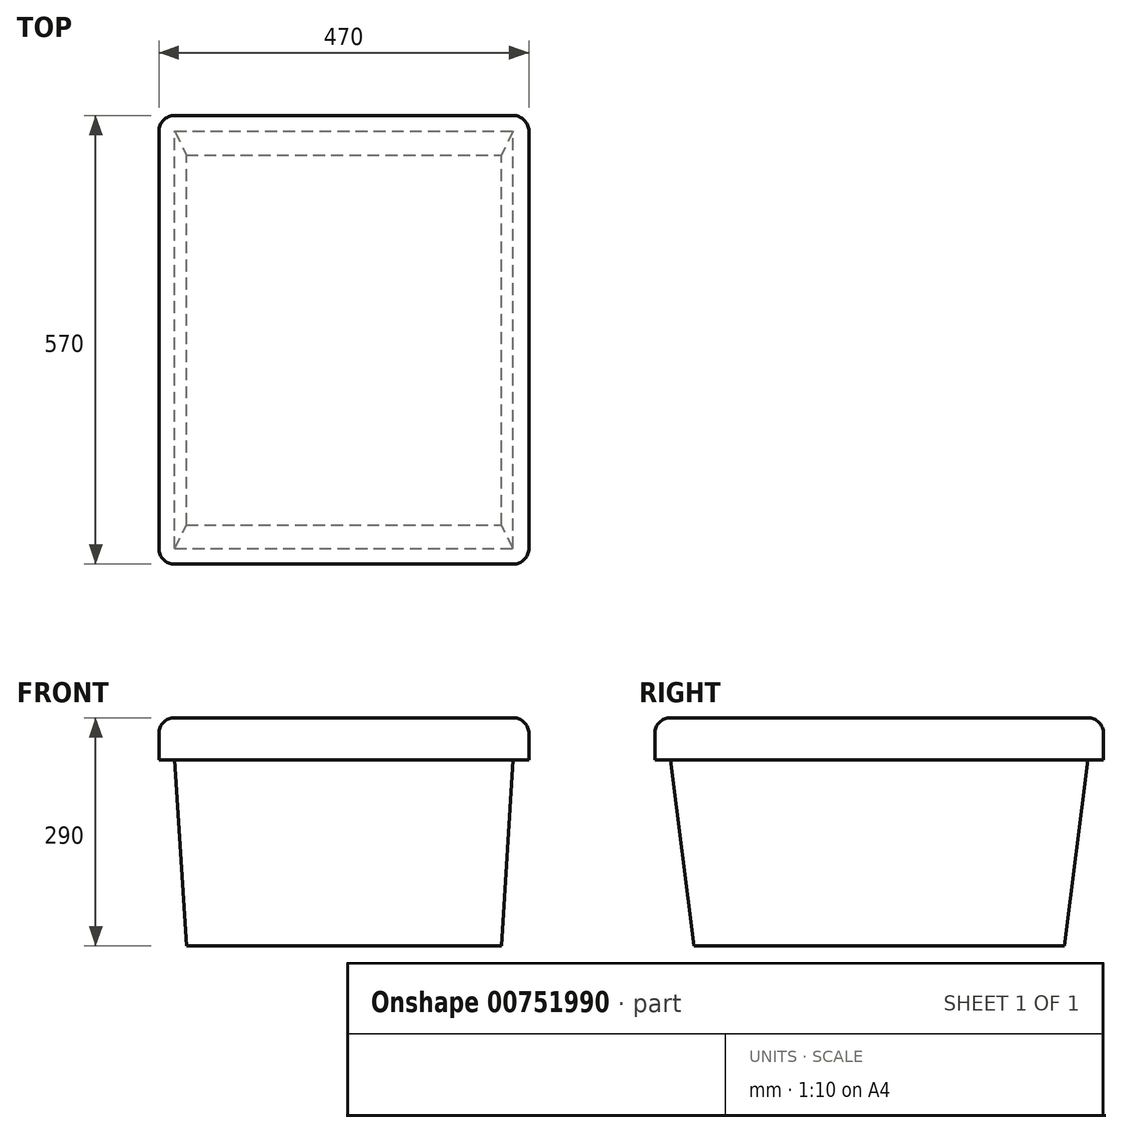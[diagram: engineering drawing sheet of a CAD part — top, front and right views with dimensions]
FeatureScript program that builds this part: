
annotation { "Feature Type Name" : "Feature", "Feature Type Description" : "" }
export const myFeature = defineFeature(function(context is Context, id is Id, definition is map)
    precondition{}
    {
        {
            var Q0;
            Q0=qCreatedBy(makeId("Front.planeOp"),FACE);
            var sketch = newSketch(context, id + "F0", { "sketchPlane" : qUnion([Q0])});
            skLineSegment(sketch, "E0.bottom", {"start": v(-35, 0) * mm, "end": v(-435, 0) * mm});
            skLineSegment(sketch, "E0.top", {"start": v(-20, 290) * mm, "end": v(-450, 290) * mm});
            skLineSegment(sketch, "E0.left", {"start": v(0, 236.3) * mm, "end": v(0, 270) * mm});
            skLineSegment(sketch, "E0.right", {"start": v(-470, 236.3) * mm, "end": v(-470, 270) * mm});
            skLineSegment(sketch, "E1", {"start": v(-470, 236.3) * mm, "end": v(-450, 236.3) * mm});
            skLineSegment(sketch, "E2", {"start": v(-450, 236.3) * mm, "end": v(-435, 0) * mm});
            skLineSegment(sketch, "E3", {"start": v(-235, 290) * mm, "end": v(-235, 0) * mm});
            skLineSegment(sketch, "E4.MirrorCS", {"start": v(-20, 236.3) * mm, "end": v(-35, 0) * mm});
            skLineSegment(sketch, "E5.MirrorCS", {"start": v(0, 236.3) * mm, "end": v(-20, 236.3) * mm});
            skPoint(sketch, "E6.orphan", {"position": v(-470, 0) * mm});
            skPoint(sketch, "E7.orphan", {"position": v(0, 0) * mm});
            skPoint(sketch, "E8.visualSharp", {"position": v(-470, 290) * mm});
            skArc(sketch, "E8.filletArc", {"start": v(-450, 290) * mm, "mid": v(-464.14, 284.14) * mm, "end": v(-470, 270) * mm});
            skPoint(sketch, "E9.visualSharp", {"position": v(0, 290) * mm});
            skArc(sketch, "E9.filletArc", {"start": v(0, 270) * mm, "mid": v(-5.86, 284.14) * mm, "end": v(-20, 290) * mm});
            skSolve(sketch);
        }
        {
            var Q0;
            Q0 = qSketchRegion(id + "F0", true);
            extrude(context, id + "F1", {"entities" : qUnion([Q0]), "depth" : 570 * mm, "offsetDistance" : 25 * mm});
        }
        {
            var Q0;
            Q0=qCreatedBy(makeId("Right.planeOp"),FACE);
            var sketch = newSketch(context, id + "F2", { "sketchPlane" : qUnion([Q0])});
            skLineSegment(sketch, "E10.0.0", {"start": v(0, 0) * mm, "end": v(0, 236.3) * mm});
            skLineSegment(sketch, "E10.0.1", {"start": v(0, 236.3) * mm, "end": v(-570, 236.3) * mm});
            skLineSegment(sketch, "E10.0.2", {"start": v(-570, 236.3) * mm, "end": v(-570, 0) * mm});
            skLineSegment(sketch, "E10.0.3", {"start": v(-570, 0) * mm, "end": v(0, 0) * mm});
            skLineSegment(sketch, "E11", {"start": v(0, 236.3) * mm, "end": v(-20, 236.3) * mm});
            skLineSegment(sketch, "E12", {"start": v(-20, 236.3) * mm, "end": v(-50, 0) * mm});
            skLineSegment(sketch, "E13", {"start": v(-285, 236.3) * mm, "end": v(-285, 0) * mm, "construction": true});
            skLineSegment(sketch, "E14.MirrorCS", {"start": v(-550, 236.3) * mm, "end": v(-520, 0) * mm});
            skLineSegment(sketch, "E15.MirrorCS", {"start": v(-570, 236.3) * mm, "end": v(0, 236.3) * mm});
            skSolve(sketch);
        }
        {
            var Q0;
            {var subQ0=sQuery(id+"F2.wireOp",EDGE,"E10.0.0");Q0=makeQuery(id+"F2.imprint","IMPRINT",FACE,{"disambiguationData":[TD([[makeQuery(id+"F2.imprint","IMPRINT",EDGE,{"derivedFrom":subQ0}),1.0]])]});}
            var Q1;
            {var subQ0=sQuery(id+"F2.wireOp",EDGE,"E10.0.2");Q1=makeQuery(id+"F2.imprint","IMPRINT",FACE,{"disambiguationData":[TD([[makeQuery(id+"F2.imprint","IMPRINT",EDGE,{"derivedFrom":subQ0}),1.0]])]});}
            extrude(context, id + "F3", {"entities" : qUnion([Q0, Q1]), "operationType" : NewBodyOperationType.REMOVE, "endBound" : BoundingType.THROUGH_ALL, "oppositeDirection" : true, "depth" : 25 * mm, "offsetDistance" : 25 * mm});
        }
        {
            var Q0;
            Q0=makeQuery(id+"F1.opExtrude","CAP_EDGE",EDGE,{"disambiguationData":[OSD([sQuery(id+"F0.wireOp",EDGE,"E0.top")])],"isStart":false});
            var Q1;
            Q1=makeQuery(id+"F1.opExtrude","CAP_EDGE",EDGE,{"disambiguationData":[OSD([sQuery(id+"F0.wireOp",EDGE,"E0.top")])],"isStart":true});
            fillet(context, id + "F4", {"entities" : qUnion([Q0, Q1]), "radius" : 20 * mm, "tangentPropagation" : true, "allowEdgeOverflow" : false});
        }
    });
